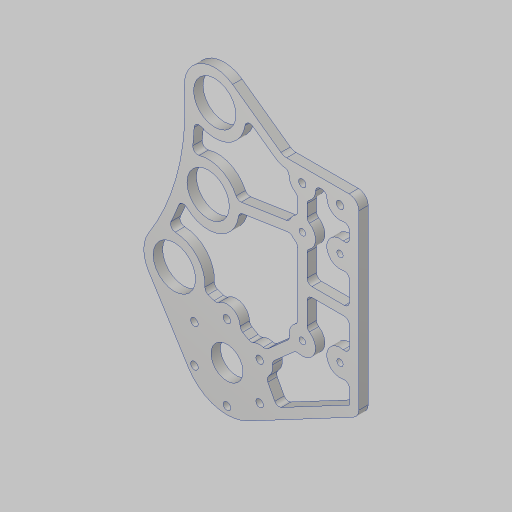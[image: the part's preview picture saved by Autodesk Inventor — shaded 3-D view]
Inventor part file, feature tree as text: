
AUTODESK INVENTOR PART (.ipt)
format: ipt  version: 2023.5 (Build 275446000, 446)  size: 436,224 bytes
history: native  units: in
note: dims shown in document units (in); Inventor stores cm internally (conversion verified against a paired STEP export)
features: sketch x4, hole x3, extrude x2, fillet x2, projected_geometry x2
ambient origin geometry x8: Origin, YZ Plane, XZ Plane, XY Plane, X Axis, Y Axis, Z Axis, Center Point
bodies: Solid1 (feature_tree)
feature tree (13):
  sketch  "Sketch1"  dims[d0=2.0in d1=15.0in]
  sketch  "Sketch2"  dims[d2=0.875in d3=17.0in]
  extrude  "Extrusion1"  Depth=2.0in
  hole  "Hole1"  [1 undecoded]
  hole  "Hole2"  [1 undecoded]
  fillet  "Fillet1"  Radius=1.0in
  hole  "Hole3"  [1 undecoded]
  extrude  "Extrusion2"  Depth=0.25in
  fillet  "Fillet2"  Radius=3.6in
  sketch  "Sketch3"  dims[d4=2.0in d5=17.0in d6=1.0in]
  projected_geometry  "Projected Loop1"
  sketch  "Sketch4"  dims[d7=0.2405in d8=2.4in d9=0.5in d10=3.6in d11=1.5in d12=1.5in d13=0.9in d14=3.7in d15=1.0in d16=3.4in d17=3.0in d20=2.0in d22=1.125in d23=4.297in d24=0.25in d25=2.0in d26=2.3622in d28=360.0deg d30=7.0in d31=2.0in d32=0.201in d33=1.0in d34=1.5in d35=1.0in d36=0.201in d37=1.0in d38=1.0in d39=2.5in d40=0.25in d41=0.0in d42=0.85in d43=0.201in d44=0.75in d45=0.385in d46=0.25in d47=0.5635in d48=1.0in d49=0.8108in d50=0.375in d51=0.171in d52=0.432in d53=0.385in d54=0.25in d55=0.5635in d56=1.0in d57=0.8108in d58=0.26in d59=1.825in d60=0.25in d61=0.25in d62=0.25in d63=1.0in d64=0.125in d65=0.125in d66=0.125in d67=0.125in d68=0.125in d69=0.125in d70=1.0in d71=0.0in d72=0.13in d74=1.75in d75=0.875in d76=0.156in d77=0.38in d78=0.375in d79=0.25in d80=0.5635in d81=1.0in d82=0.8108in d83=0.125in d84=0.125in]
  projected_geometry  "Projected Loop2"
note: 3 required parameter values undecoded (feature->parameter linkage not recoverable at this tier; creation-order binding heuristic only, values carry confidence <= 0.55)
